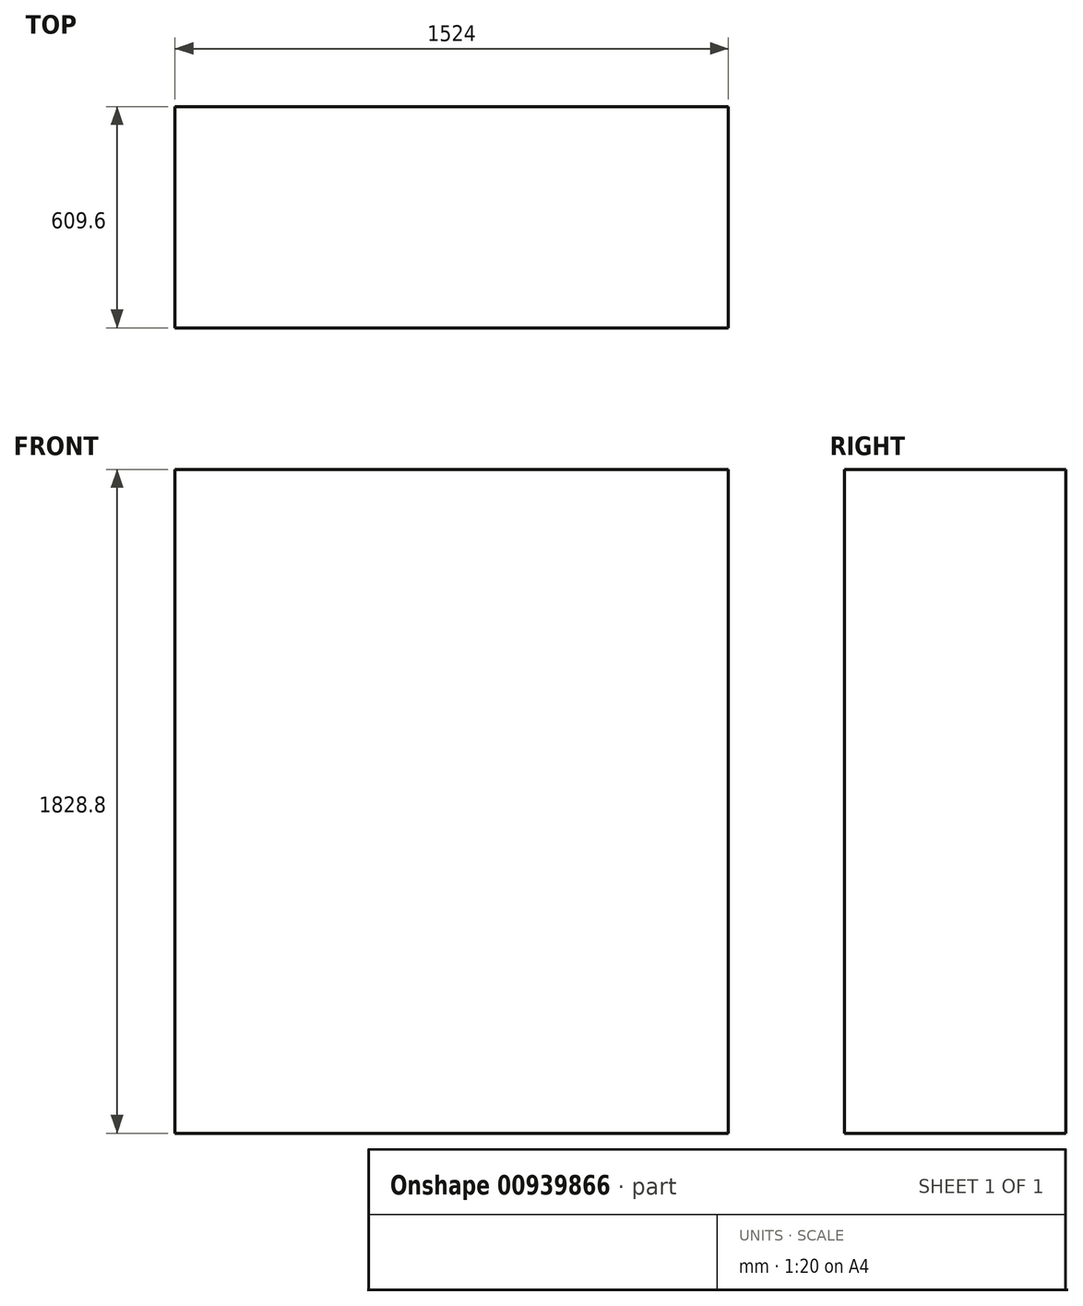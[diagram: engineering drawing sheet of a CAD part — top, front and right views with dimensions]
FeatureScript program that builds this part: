
annotation { "Feature Type Name" : "Feature", "Feature Type Description" : "" }
export const myFeature = defineFeature(function(context is Context, id is Id, definition is map)
    precondition{}
    {
        {
            var Q0;
            Q0=qCreatedBy(makeId("Top.planeOp"),FACE);
            var sketch = newSketch(context, id + "F0", { "sketchPlane" : qUnion([Q0])});
            skLineSegment(sketch, "E0.bottom", {"start": v(762, 304.8) * mm, "end": v(-762, 304.8) * mm});
            skLineSegment(sketch, "E0.top", {"start": v(762, -304.8) * mm, "end": v(-762, -304.8) * mm});
            skLineSegment(sketch, "E0.left", {"start": v(762, 304.8) * mm, "end": v(762, -304.8) * mm});
            skLineSegment(sketch, "E0.right", {"start": v(-762, 304.8) * mm, "end": v(-762, -304.8) * mm});
            skPoint(sketch, "E0.middle", {"position": v(0, 0) * mm});
            skSolve(sketch);
        }
        {
            var Q0;
            Q0 = qSketchRegion(id + "F0", true);
            extrude(context, id + "F1", {"entities" : qUnion([Q0]), "depth" : 1828.8 * mm, "offsetDistance" : 25.4 * mm});
        }
    });
